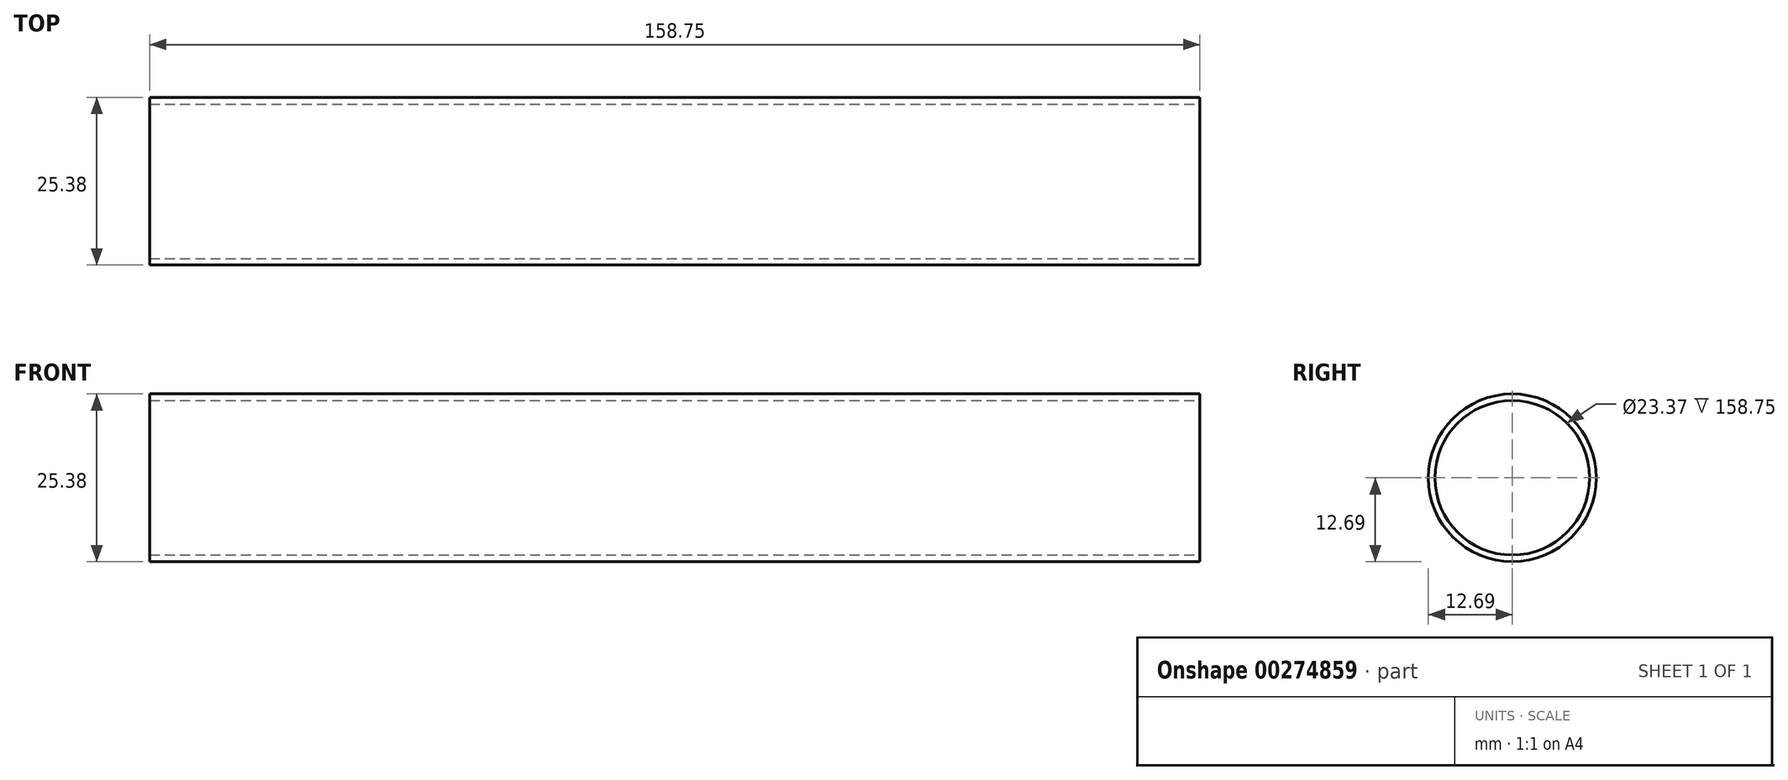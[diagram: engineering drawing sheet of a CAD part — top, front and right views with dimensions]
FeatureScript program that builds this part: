
annotation { "Feature Type Name" : "Feature", "Feature Type Description" : "" }
export const myFeature = defineFeature(function(context is Context, id is Id, definition is map)
    precondition{}
    {
        {
            var Q0;
            Q0=qCreatedBy(makeId("Right.planeOp"),FACE);
            var sketch = newSketch(context, id + "F0", { "sketchPlane" : qUnion([Q0])});
            skCircle(sketch, "E0", {"center": v(0, 0) * mm, "radius": 12.69 * mm});
            skSolve(sketch);
        }
        {
            var Q0;
            Q0=makeQuery(id+"F0.imprint","IMPRINT",FACE,{"disambiguationData":[TD([[makeQuery(id+"F0.imprint","IMPRINT",EDGE,{"derivedFrom":sQuery(id+"F0.wireOp",EDGE,"E0")}),1.0]])]});
            extrude(context, id + "F1", {"entities" : qUnion([Q0]), "depth" : 158.75 * mm});
        }
        {
            var Q0;
            Q0=qCreatedBy(makeId("Right.planeOp"),FACE);
            var sketch = newSketch(context, id + "F2", { "sketchPlane" : qUnion([Q0])});
            skPoint(sketch, "E1", {"position": v(0, 0) * mm});
            skSolve(sketch);
        }
        {
            var Q0;
            Q0=sQuery(id+"F2.wireOp",VERTEX,"E1");
            var Q1;
            Q1=makeQuery(id+"F1.opExtrude","SWEPT_BODY",BODY,{"disambiguationData":[OSD([sQuery(id+"F0.wireOp",EDGE,"E0")])]});
            hole(context, id + "F3", {"style" : HoleStyle.SIMPLE, "endStyle" : HoleEndStyle.THROUGH, "oppositeDirection" : true, "holeDiameter" : 23.37 * mm, "tappedDepth" : 12.7 * mm, "tapClearance" : 3, "locations" : qUnion([Q0]), "scope" : qUnion([Q1]), "startStyle" : HoleStartStyle.SKETCH});
        }
    });
